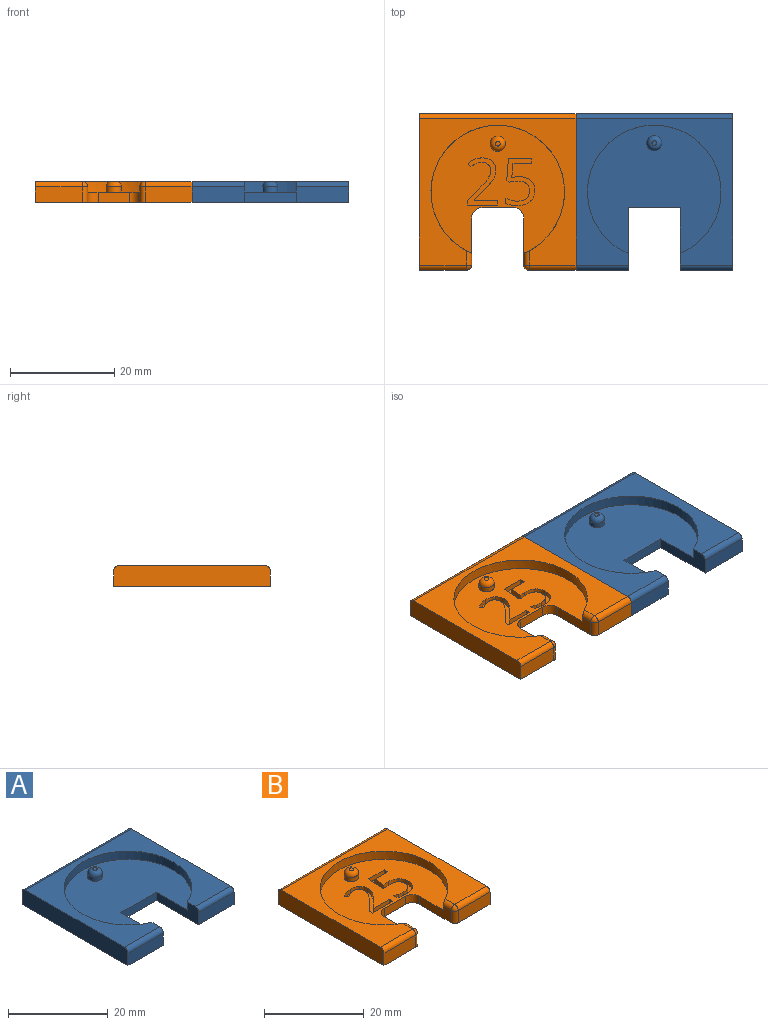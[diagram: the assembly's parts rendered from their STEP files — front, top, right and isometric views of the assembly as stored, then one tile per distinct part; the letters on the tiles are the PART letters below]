
ASSEMBLY  parts=2 mates=1
PART A: 18 faces, bbox 30x30x4 mm
  f0: plane 10x3mm, normal (0,-1,0), area 30mm2, adj f3,f7,f10,f17
  f1: plane 25.6x24.58mm, normal (0,0,1), area 413.4mm2, adj f10,f11,f12,f13,f16
  f2: plane 30x28mm, normal (0,0,1), area 309.9mm2, adj f3,f4,f5,f7,f9,f10,f11,f12
  f3: cylinder r=1mm len=10mm, axis (-1,0,0), area 15.7mm2, adj f0,f2,f7,f10
  f4: cylinder r=1mm len=10mm, axis (-1,0,0), area 15.7mm2, adj f2,f5,f6,f12
  f5: plane 30x4mm, normal (-1,0,0), area 119.6mm2, adj f2,f4,f6,f8,f9,f17
  f6: plane 10x3mm, normal (0,-1,0), area 30mm2, adj f4,f5,f12,f17
  f7: plane 30x4mm, normal (1,0,0), area 119.6mm2, adj f0,f2,f3,f8,f9,f17
  f8: plane 30x3mm, normal (0,1,0), area 90mm2, adj f5,f7,f9,f17
  f9: cylinder r=1mm len=30mm, axis (1,0,0), area 47.1mm2, adj f2,f5,f7,f8
  f10: plane 12x4mm, normal (-1,0,0), area 30.2mm2, adj f0,f1,f2,f3,f11,f16,f17
  f11: cylinder r=12.8mm len=25.6mm, axis (0,0,1), area 140.3mm2, adj f1,f2,f10,f12
  f12: plane 12x4mm, normal (1,0,0), area 30.2mm2, adj f1,f2,f4,f6,f11,f16,f17
  f13: cylinder r=1.45mm len=2.9mm, axis (0,0,-1), area 9.1mm2, adj f1,f15
  f14: plane 0.9x0.9mm, normal (0,0,1), area 0.6mm2, adj f15
  f15: torus R=0.45mm, axis (0,0,1), area 10.7mm2, adj f13,f14
  f16: plane 10x2mm, normal (0,-1,0), area 20mm2, adj f1,f10,f12,f17
  f17: plane 30x30mm, normal (0,0,-1), area 780mm2, adj f0,f5,f6,f7,f8,f10,f12,f16
PART B: 67 faces, bbox 30x30x4 mm
  f0: plane 25.6x24.58mm, normal (0,0,1), area 379.3mm2, adj f10,f11,f12,f13,f16,f18,f19,f20
  f1: plane 9x3mm, normal (0,-1,0), area 27mm2, adj f3,f7,f17,f64
  f2: plane 30x28mm, normal (0,0,1), area 305.1mm2, adj f3,f4,f5,f7,f9,f11,f63,f66
  f3: cylinder r=1mm len=9mm, axis (-1,0,0), area 14.1mm2, adj f1,f2,f7,f65
  f4: cylinder r=1mm len=9mm, axis (-1,0,0), area 14.1mm2, adj f2,f5,f6,f62
  f5: plane 30x4mm, normal (-1,0,0), area 119.6mm2, adj f2,f4,f6,f8,f9,f17
  f6: plane 9x3mm, normal (0,-1,0), area 27mm2, adj f4,f5,f17,f61
  f7: plane 30x4mm, normal (1,0,0), area 119.6mm2, adj f1,f2,f3,f8,f9,f17
  f8: plane 30x3mm, normal (0,1,0), area 90mm2, adj f5,f7,f9,f17
  f9: cylinder r=1mm len=30mm, axis (1,0,0), area 47.1mm2, adj f2,f5,f7,f8
  f10: plane 9x3mm, normal (-1,0,0), area 20.2mm2, adj f0,f11,f17,f59,f64,f66
  f11: cylinder r=12.8mm len=25.6mm, axis (0,0,1), area 139.8mm2, adj f0,f2,f10,f12,f63,f66
  f12: plane 9x3mm, normal (1,0,0), area 20.2mm2, adj f0,f11,f17,f60,f61,f63
  f13: cylinder r=1.45mm len=2.9mm, axis (0,0,-1), area 9.1mm2, adj f0,f15
  f14: plane 0.9x0.9mm, normal (0,0,1), area 0.6mm2, adj f15
  f15: torus R=0.45mm, axis (0,0,1), area 10.7mm2, adj f13,f14
  f16: plane 6x2mm, normal (0,-1,0), area 12mm2, adj f0,f17,f59,f60
  f17: plane 30x30mm, normal (0,0,-1), area 781.3mm2, adj f1,f5,f6,f7,f8,f10,f12,f16
  f18: extruded ~2.21x1mm, area 2.4mm2, adj f0,f19,f36,f37
  f19: extruded ~1.39x1mm, area 1.4mm2, adj f0,f18,f20,f37
  f20: plane 2.67x1mm, normal (-1,0.08,0), area 2.7mm2, adj f0,f19,f21,f37
  f21: plane 3.56x1mm, normal (0,1,0), area 3.6mm2, adj f0,f20,f22,f37
  f22: plane 1x0.93mm, normal (-1,0,0), area 0.9mm2, adj f0,f21,f23,f37
  f23: plane 4.42x1mm, normal (0,-1,0), area 4.4mm2, adj f0,f22,f24,f37
  f24: plane 4.16x1mm, normal (1,-0.08,0), area 4.2mm2, adj f0,f23,f25,f37
  f25: plane 1x0.52mm, normal (0.54,0.84,0), area 0.6mm2, adj f0,f24,f26,f37
  f26: extruded ~1.55x1mm, area 1.6mm2, adj f0,f25,f27,f37
  f27: extruded ~2.28x1.86mm, area 3.4mm2, adj f0,f26,f28,f37
  f28: extruded ~1.46x1mm, area 1.6mm2, adj f0,f27,f29,f37
  f29: extruded ~1.66x1mm, area 1.8mm2, adj f0,f28,f30,f37
  f30: extruded ~1.25x1mm, area 1.3mm2, adj f0,f29,f31,f37
  f31: extruded ~1.06x1mm, area 1.1mm2, adj f0,f30,f32,f37
  f32: plane 1x0.97mm, normal (1,0,0), area 1mm2, adj f0,f31,f33,f37
  f33: extruded ~2.29x1mm, area 2.4mm2, adj f0,f32,f34,f37
  f34: extruded ~2.43x1mm, area 2.6mm2, adj f0,f33,f35,f37
  f35: extruded ~2.17x1mm, area 2.4mm2, adj f0,f34,f36,f37
  f36: extruded ~1.91x1mm, area 2.1mm2, adj f0,f18,f35,f37
  f37: plane 9.02x5.6mm, normal (0,0,1), area 18.4mm2, adj f18,f19,f20,f21,f22,f23,f24,f25
  f38: plane 5.85x1mm, normal (0,1,0), area 5.8mm2, adj f0,f39,f57,f58
  f39: plane 1x0.94mm, normal (-1,0,0), area 0.9mm2, adj f0,f38,f40,f58
  f40: plane 4.58x1mm, normal (0,-1,0), area 4.6mm2, adj f0,f39,f41,f58
  f41: plane 1x0.05mm, normal (-1,0,0), area 0mm2, adj f0,f40,f42,f58
  f42: plane 1.95x1.9mm, normal (-0.7,0.71,0), area 2.7mm2, adj f0,f41,f43,f58
  f43: extruded ~2.09x1.78mm, area 2.8mm2, adj f0,f42,f44,f58
  f44: extruded ~1.68x1mm, area 1.8mm2, adj f0,f43,f45,f58
  f45: extruded ~1.72x1mm, area 1.9mm2, adj f0,f44,f46,f58
  f46: extruded ~1.97x1mm, area 2.1mm2, adj f0,f45,f47,f58
  f47: extruded ~2.68x1.02mm, area 2.9mm2, adj f0,f46,f48,f58
  f48: plane 1x0.69mm, normal (0.79,0.61,0), area 0.9mm2, adj f0,f47,f49,f58
  f49: extruded ~1.1x1mm, area 1.3mm2, adj f0,f48,f50,f58
  f50: extruded ~1.05x1mm, area 1.1mm2, adj f0,f49,f51,f58
  f51: extruded ~1.2x1mm, area 1.3mm2, adj f0,f50,f52,f58
  f52: extruded ~1.13x1mm, area 1.2mm2, adj f0,f51,f53,f58
  f53: extruded ~1x0.94mm, area 1mm2, adj f0,f52,f54,f58
  f54: extruded ~1x0.9mm, area 1mm2, adj f0,f53,f55,f58
  f55: extruded ~1.55x1.41mm, area 2.1mm2, adj f0,f54,f56,f58
  f56: plane 2.35x2.34mm, normal (0.71,-0.71,0), area 3.3mm2, adj f0,f55,f57,f58
  f57: plane 1x0.87mm, normal (1,0,0), area 0.9mm2, adj f0,f38,f56,f58
  f58: plane 9.02x5.85mm, normal (0,0,1), area 17.4mm2, adj f38,f39,f40,f41,f42,f43,f44,f45
  f59: cylinder r=2mm len=2mm, axis (0,0,-1), area 6.3mm2, adj f0,f10,f16,f17
  f60: cylinder r=2mm len=2mm, axis (0,0,-1), area 6.3mm2, adj f0,f12,f16,f17
  f61: cylinder r=1mm len=3mm, axis (0,0,-1), area 4.7mm2, adj f6,f12,f17,f62
  f62: sphere r=1mm, area 1.6mm2, adj f4,f61,f63
  f63: cylinder r=1mm len=2.69mm, axis (0,1,0), area 3.7mm2, adj f2,f11,f12,f62
  f64: cylinder r=1mm len=3mm, axis (0,0,-1), area 4.7mm2, adj f1,f10,f17,f65
  f65: sphere r=1mm, area 1.6mm2, adj f3,f64,f66
  f66: cylinder r=1mm len=2.69mm, axis (0,-1,0), area 3.7mm2, adj f2,f10,f11,f65
PLACE A t=(33.87,-19.53,16.16)mm
PLACE B t=(3.87,-19.53,16.16)mm
MATE fastened A.f5 <-> B.f7  axis (1,0,0) through (-25.85,-27.15,15.16)mm
